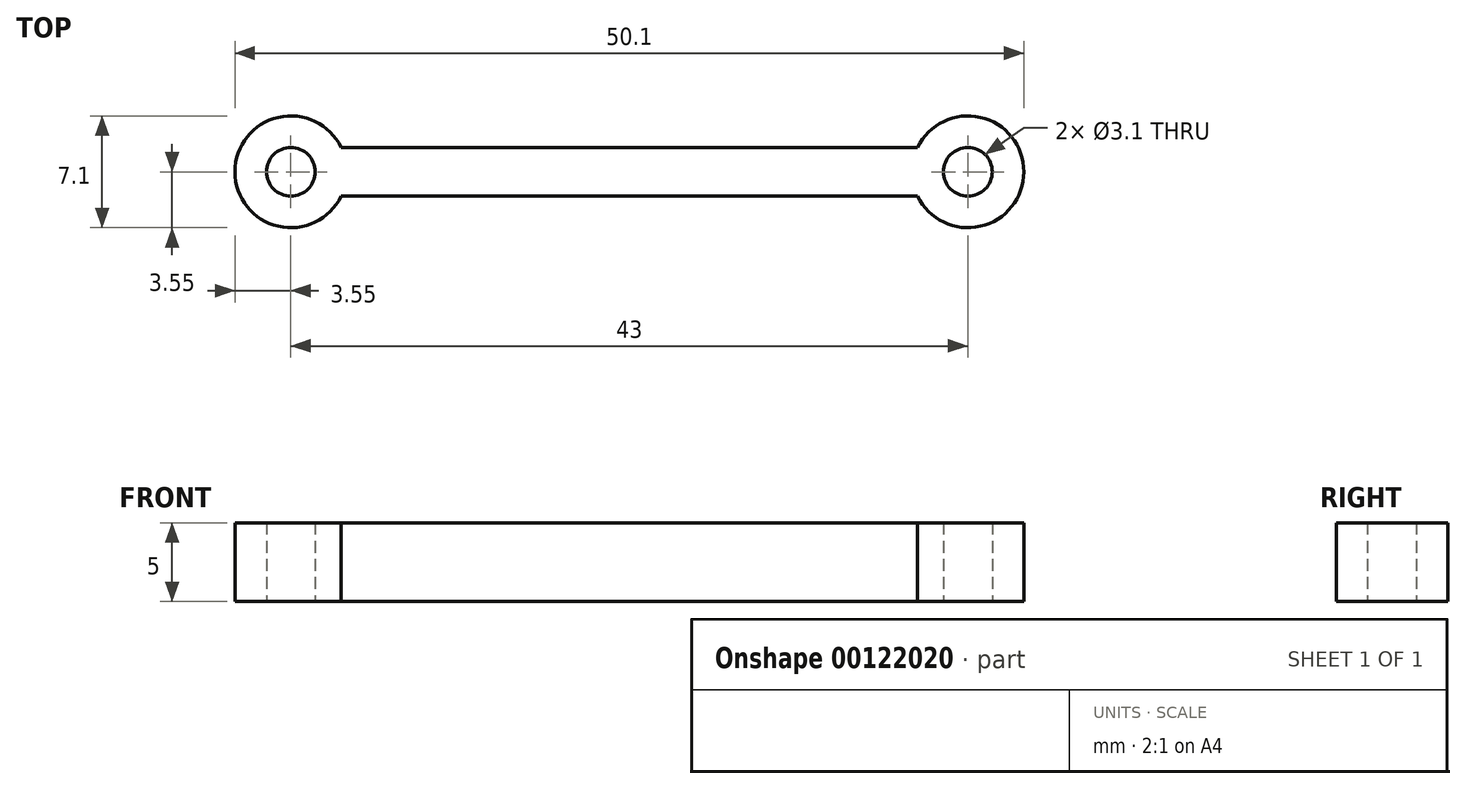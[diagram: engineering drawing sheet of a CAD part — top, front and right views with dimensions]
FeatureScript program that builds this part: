
annotation { "Feature Type Name" : "Feature", "Feature Type Description" : "" }
export const myFeature = defineFeature(function(context is Context, id is Id, definition is map)
    precondition{}
    {
        {
            var Q0;
            Q0=qCreatedBy(makeId("Top.planeOp"),FACE);
            var sketch = newSketch(context, id + "F0", { "sketchPlane" : qUnion([Q0])});
            skArc(sketch, "E0.0", {"start": v(-18.3, 1.55) * mm, "mid": v(-25.05, 0) * mm, "end": v(-18.3, -1.55) * mm});
            skArc(sketch, "E1.0", {"start": v(18.3, -1.55) * mm, "mid": v(25.05, 0) * mm, "end": v(18.3, 1.55) * mm});
            skLineSegment(sketch, "E2", {"start": v(-18.3, 1.55) * mm, "end": v(18.3, 1.55) * mm});
            skLineSegment(sketch, "E3", {"start": v(18.3, -1.55) * mm, "end": v(-18.3, -1.55) * mm});
            skCircle(sketch, "E4", {"center": v(-21.5, 0) * mm, "radius": 1.55 * mm});
            skCircle(sketch, "E5", {"center": v(21.5, 0) * mm, "radius": 1.55 * mm});
            skSolve(sketch);
        }
        {
            var Q0;
            Q0=makeQuery(id+"F0.imprint","IMPRINT",FACE,{"disambiguationData":[TD([[makeQuery(id+"F0.imprint","IMPRINT",EDGE,{"derivedFrom":sQuery(id+"F0.wireOp",EDGE,"E0.0")}),1.0]])]});
            extrude(context, id + "F1", {"entities" : qUnion([Q0]), "depth" : 5 * mm});
        }
    });
